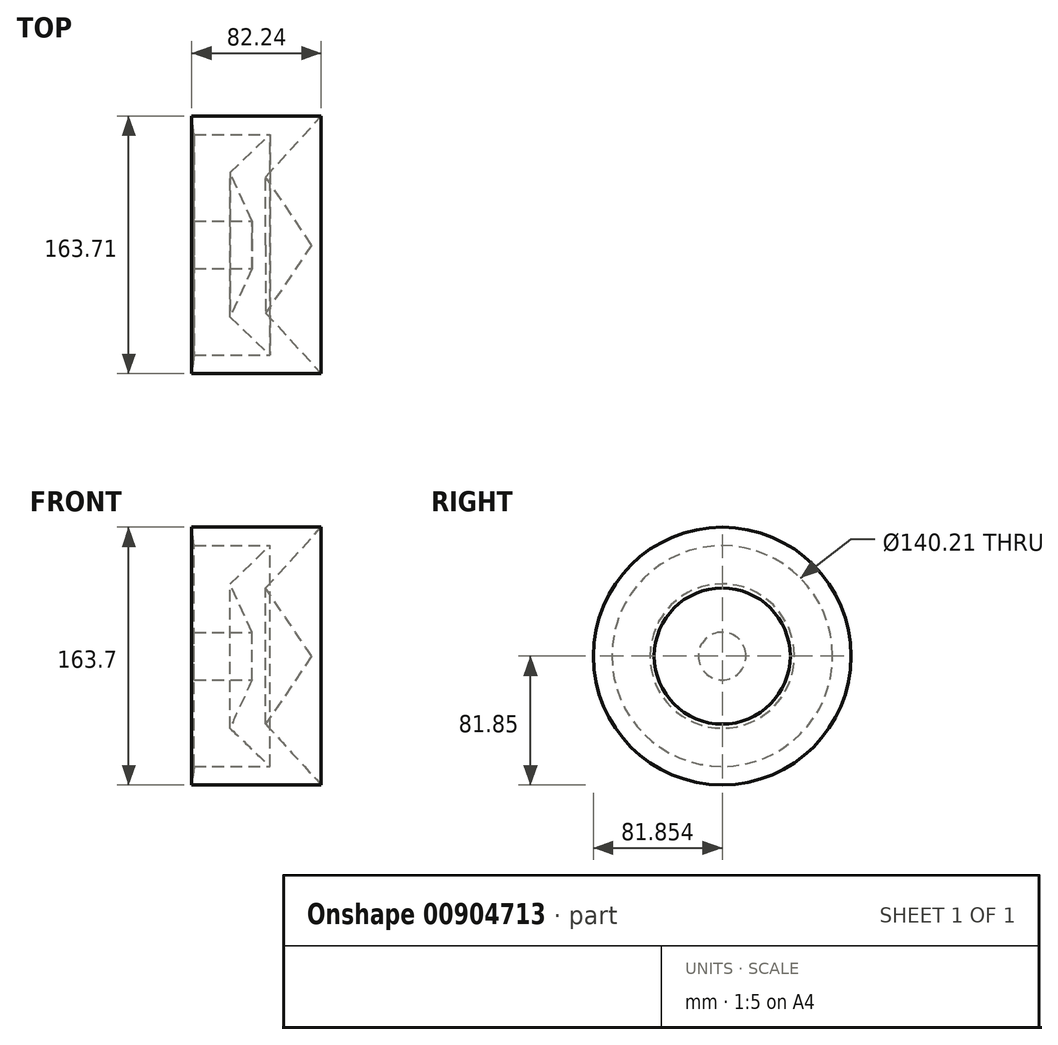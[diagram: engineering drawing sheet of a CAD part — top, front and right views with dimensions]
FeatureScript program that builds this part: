
annotation { "Feature Type Name" : "Feature", "Feature Type Description" : "" }
export const myFeature = defineFeature(function(context is Context, id is Id, definition is map)
    precondition{}
    {
        {
            var Q0;
            Q0=qCreatedBy(makeId("Top.planeOp"),FACE);
            var sketch = newSketch(context, id + "F0", { "sketchPlane" : qUnion([Q0])});
            skLineSegment(sketch, "E0", {"start": v(-30.13, -50.6) * mm, "end": v(52.1, -50.6) * mm});
            skLineSegment(sketch, "E1", {"start": v(52.1, -50.6) * mm, "end": v(16.86, -11.94) * mm});
            skLineSegment(sketch, "E2", {"start": v(16.86, -11.94) * mm, "end": v(46.04, 31.26) * mm});
            skLineSegment(sketch, "E3", {"start": v(46.04, 31.26) * mm, "end": v(-28.61, 31.26) * mm});
            skLineSegment(sketch, "E4", {"start": v(-28.61, 31.26) * mm, "end": v(-28.61, 16.1) * mm});
            skLineSegment(sketch, "E5", {"start": v(-28.61, 16.1) * mm, "end": v(8.15, 16.1) * mm});
            skLineSegment(sketch, "E6", {"start": v(8.15, 16.1) * mm, "end": v(-5.87, -14.59) * mm});
            skLineSegment(sketch, "E7", {"start": v(-5.87, -14.59) * mm, "end": v(19.52, -38.84) * mm});
            skLineSegment(sketch, "E8", {"start": v(19.52, -38.84) * mm, "end": v(-28.61, -38.84) * mm});
            skLineSegment(sketch, "E9", {"start": v(-28.61, -38.84) * mm, "end": v(-30.13, -50.6) * mm});
            skSolve(sketch);
        }
        {
            var Q0;
            Q0 = qSketchRegion(id + "F0", true);
            var Q1;
            Q1=sQuery(id+"F0.wireOp",EDGE,"E3");
            revolve(context, id + "F1", {"surfaceOperationType" : NewSurfaceOperationType.NEW, "entities" : qUnion([Q0]), "axis" : qUnion([Q1]), "revolveType" : RevolveType.FULL});
        }
    });
